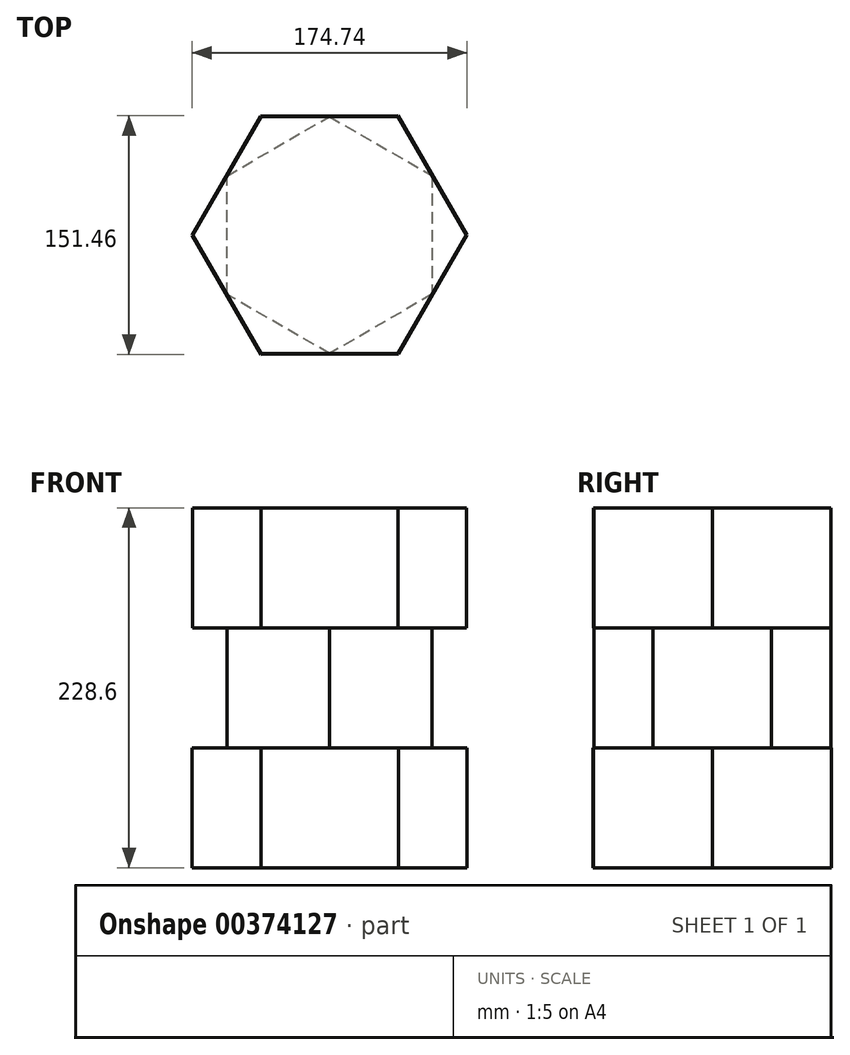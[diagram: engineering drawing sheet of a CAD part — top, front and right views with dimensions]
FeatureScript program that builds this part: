
annotation { "Feature Type Name" : "Feature", "Feature Type Description" : "" }
export const myFeature = defineFeature(function(context is Context, id is Id, definition is map)
    precondition{}
    {
        {
            var Q0;
            Q0=qCreatedBy(makeId("Top.planeOp"),FACE);
            var sketch = newSketch(context, id + "F0", { "sketchPlane" : qUnion([Q0])});
            skCircle(sketch, "E0.cCircle", {"center": v(0, 0) * mm, "radius": 75.67 * mm, "construction": true});
            skLineSegment(sketch, "E0.0", {"start": v(87.37, 0.12) * mm, "end": v(43.79, -75.6) * mm});
            skLineSegment(sketch, "E0.1", {"start": v(43.79, -75.6) * mm, "end": v(-43.59, -75.73) * mm});
            skLineSegment(sketch, "E0.2", {"start": v(-43.59, -75.73) * mm, "end": v(-87.37, -0.12) * mm});
            skLineSegment(sketch, "E0.3", {"start": v(-87.37, -0.12) * mm, "end": v(-43.79, 75.6) * mm});
            skLineSegment(sketch, "E0.4", {"start": v(-43.79, 75.6) * mm, "end": v(43.59, 75.73) * mm});
            skLineSegment(sketch, "E0.5", {"start": v(43.59, 75.73) * mm, "end": v(87.37, 0.12) * mm});
            skPoint(sketch, "E0.0.midPoint", {"position": v(65.58, -37.75) * mm});
            skSolve(sketch);
        }
        {
            var Q0;
            Q0 = qSketchRegion(id + "F0", true);
            extrude(context, id + "F1", {"entities" : qUnion([Q0]), "depth" : 76.2 * mm});
        }
        {
            var Q0;
            Q0=makeQuery(id+"F1.opExtrude","CAP_FACE",FACE,{"disambiguationData":[OSD([sQuery(id+"F0.wireOp",EDGE,"E0.0"),sQuery(id+"F0.wireOp",EDGE,"E0.1"),sQuery(id+"F0.wireOp",EDGE,"E0.2"),sQuery(id+"F0.wireOp",EDGE,"E0.3"),sQuery(id+"F0.wireOp",EDGE,"E0.4"),sQuery(id+"F0.wireOp",EDGE,"E0.5")])],"isStart":false});
            var sketch = newSketch(context, id + "F2", { "sketchPlane" : qUnion([Q0])});
            skCircle(sketch, "E1.cCircle", {"center": v(0, 0) * mm, "radius": 65.17 * mm, "construction": true});
            skLineSegment(sketch, "E1.0", {"start": v(-65.2, 37.55) * mm, "end": v(-0.08, 75.25) * mm});
            skLineSegment(sketch, "E1.1", {"start": v(-0.08, 75.25) * mm, "end": v(65.13, 37.7) * mm});
            skLineSegment(sketch, "E1.2", {"start": v(65.13, 37.7) * mm, "end": v(65.2, -37.55) * mm});
            skLineSegment(sketch, "E1.3", {"start": v(65.2, -37.55) * mm, "end": v(0.08, -75.25) * mm});
            skLineSegment(sketch, "E1.4", {"start": v(0.08, -75.25) * mm, "end": v(-65.13, -37.7) * mm});
            skLineSegment(sketch, "E1.5", {"start": v(-65.13, -37.7) * mm, "end": v(-65.2, 37.55) * mm});
            skPoint(sketch, "E1.0.midPoint", {"position": v(-32.65, 56.4) * mm});
            skSolve(sketch);
        }
        {
            var Q0;
            Q0 = qSketchRegion(id + "F2", true);
            extrude(context, id + "F3", {"entities" : qUnion([Q0]), "operationType" : NewBodyOperationType.ADD, "depth" : 76.2 * mm});
        }
        {
            var Q0;
            Q0=makeQuery(id+"F3.opExtrude","CAP_FACE",FACE,{"disambiguationData":[OSD([sQuery(id+"F2.wireOp",EDGE,"E1.0"),sQuery(id+"F2.wireOp",EDGE,"E1.1"),sQuery(id+"F2.wireOp",EDGE,"E1.2"),sQuery(id+"F2.wireOp",EDGE,"E1.3"),sQuery(id+"F2.wireOp",EDGE,"E1.4"),sQuery(id+"F2.wireOp",EDGE,"E1.5")])],"isStart":false});
            var sketch = newSketch(context, id + "F4", { "sketchPlane" : qUnion([Q0])});
            skCircle(sketch, "E2.cCircle", {"center": v(0, 0) * mm, "radius": 75.25 * mm, "construction": true});
            skLineSegment(sketch, "E2.0", {"start": v(86.89, 0.1) * mm, "end": v(43.53, -75.2) * mm});
            skLineSegment(sketch, "E2.1", {"start": v(43.53, -75.2) * mm, "end": v(-43.36, -75.3) * mm});
            skLineSegment(sketch, "E2.2", {"start": v(-43.36, -75.3) * mm, "end": v(-86.89, -0.1) * mm});
            skLineSegment(sketch, "E2.3", {"start": v(-86.89, -0.1) * mm, "end": v(-43.53, 75.2) * mm});
            skLineSegment(sketch, "E2.4", {"start": v(-43.53, 75.2) * mm, "end": v(43.36, 75.3) * mm});
            skLineSegment(sketch, "E2.5", {"start": v(43.36, 75.3) * mm, "end": v(86.89, 0.1) * mm});
            skPoint(sketch, "E2.0.midPoint", {"position": v(65.2, -37.55) * mm});
            skSolve(sketch);
        }
        {
            var Q0;
            Q0 = qSketchRegion(id + "F4", true);
            extrude(context, id + "F5", {"entities" : qUnion([Q0]), "operationType" : NewBodyOperationType.ADD, "depth" : 76.2 * mm});
        }
    });
